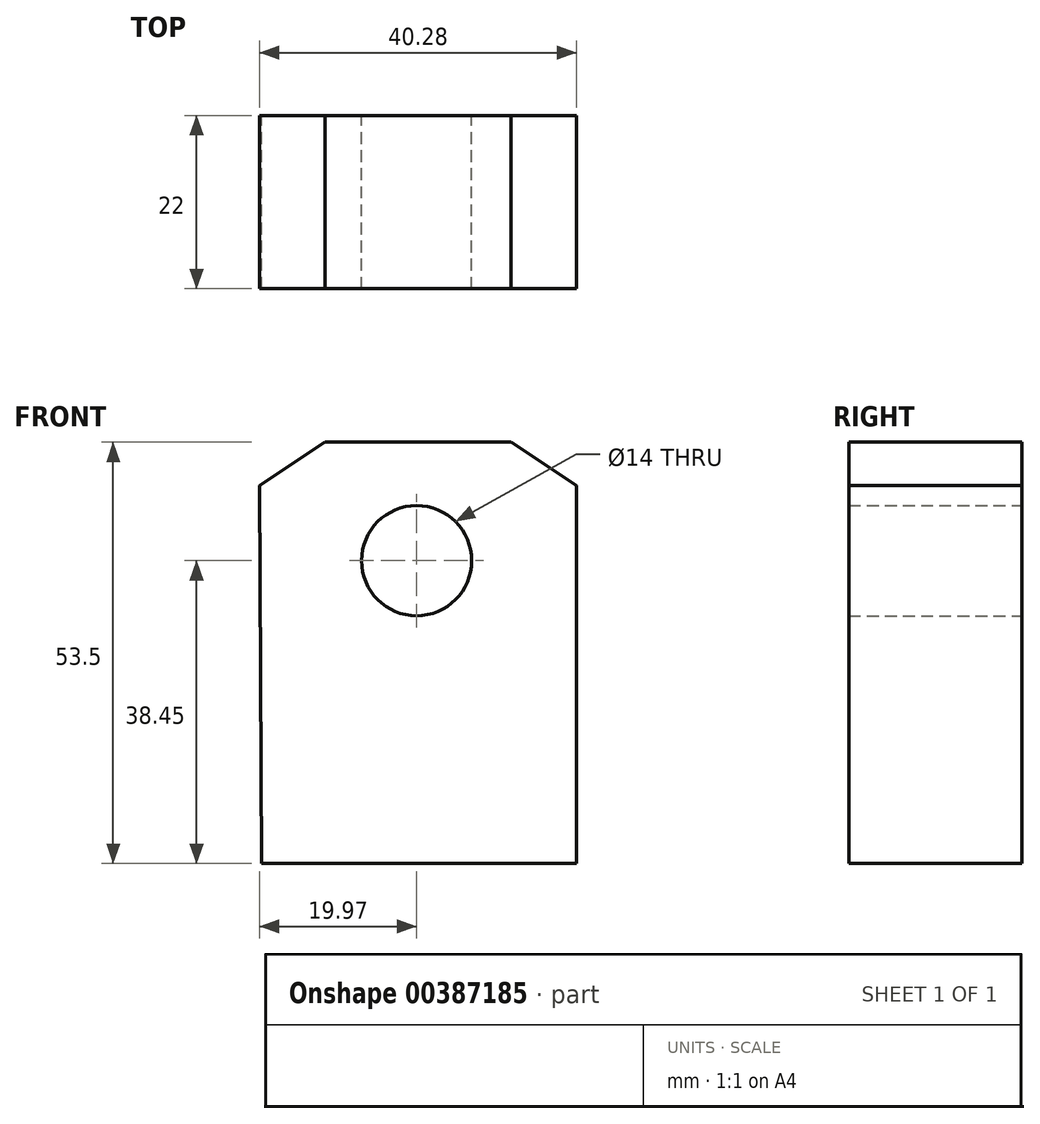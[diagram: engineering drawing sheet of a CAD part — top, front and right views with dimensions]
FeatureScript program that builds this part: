
annotation { "Feature Type Name" : "Feature", "Feature Type Description" : "" }
export const myFeature = defineFeature(function(context is Context, id is Id, definition is map)
    precondition{}
    {
        {
            var Q0;
            Q0=qCreatedBy(makeId("Front.planeOp"),FACE);
            var sketch = newSketch(context, id + "F0", { "sketchPlane" : qUnion([Q0])});
            skCircle(sketch, "E0", {"center": v(0, 0) * mm, "radius": 7 * mm});
            skLineSegment(sketch, "E1", {"start": v(-19.7, -38.45) * mm, "end": v(20.3, -38.45) * mm});
            skLineSegment(sketch, "E2", {"start": v(20.3, -38.45) * mm, "end": v(20.3, 9.53) * mm});
            skLineSegment(sketch, "E3", {"start": v(-19.7, -38.45) * mm, "end": v(-19.97, 9.53) * mm});
            skLineSegment(sketch, "E4", {"start": v(-19.97, 9.53) * mm, "end": v(-11.62, 15.05) * mm});
            skLineSegment(sketch, "E5", {"start": v(-11.62, 15.05) * mm, "end": v(11.96, 15.05) * mm});
            skLineSegment(sketch, "E6", {"start": v(11.96, 15.05) * mm, "end": v(20.3, 9.53) * mm});
            skSolve(sketch);
        }
        {
            var Q0;
            Q0 = qSketchRegion(id + "F0", true);
            extrude(context, id + "F1", {"entities" : qUnion([Q0]), "depth" : 22 * mm});
        }
    });
